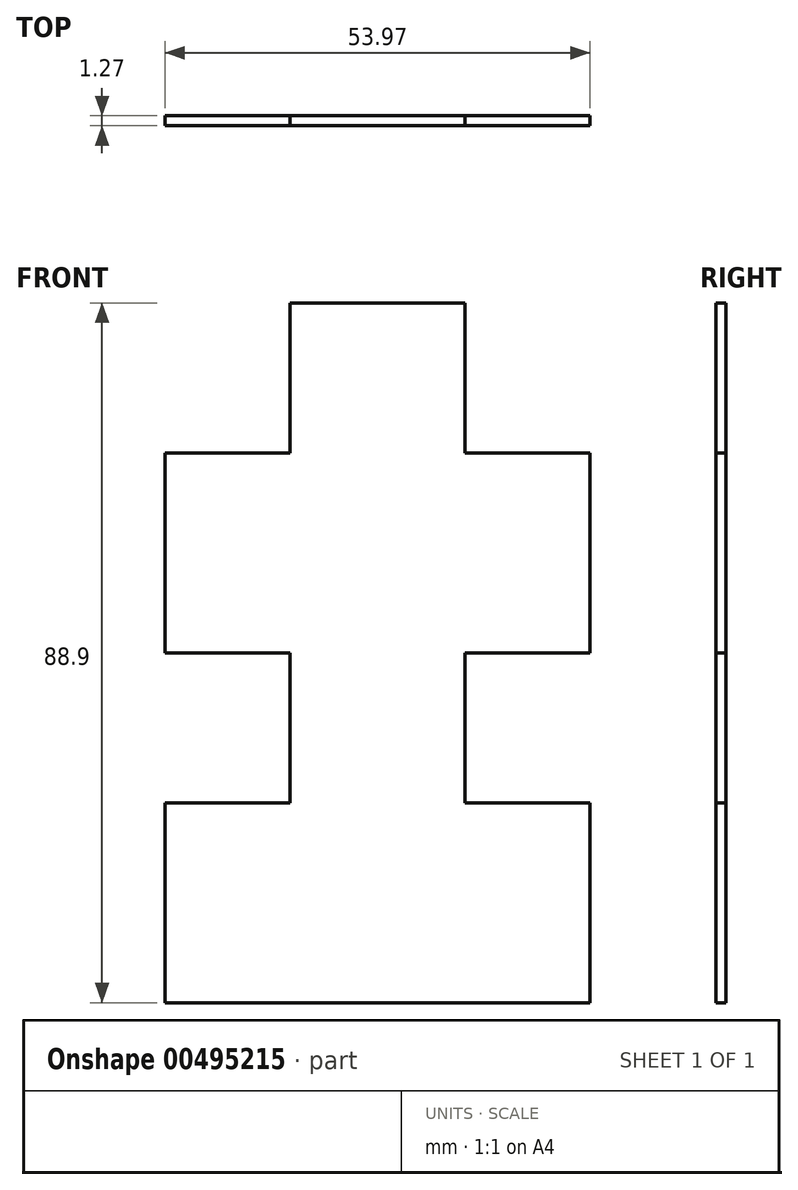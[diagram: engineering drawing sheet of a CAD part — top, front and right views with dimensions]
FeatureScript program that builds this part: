
annotation { "Feature Type Name" : "Feature", "Feature Type Description" : "" }
export const myFeature = defineFeature(function(context is Context, id is Id, definition is map)
    precondition{}
    {
        {
            var Q0;
            Q0=qCreatedBy(makeId("Front.planeOp"),FACE);
            var sketch = newSketch(context, id + "F0", { "sketchPlane" : qUnion([Q0])});
            skLineSegment(sketch, "E0", {"start": v(0.95, 45.3) * mm, "end": v(23.18, 45.3) * mm});
            skLineSegment(sketch, "E1", {"start": v(23.18, 45.3) * mm, "end": v(23.18, 26.25) * mm});
            skLineSegment(sketch, "E2", {"start": v(23.18, 26.25) * mm, "end": v(39.05, 26.25) * mm});
            skLineSegment(sketch, "E3", {"start": v(39.05, 26.25) * mm, "end": v(39.05, 0.85) * mm});
            skLineSegment(sketch, "E4", {"start": v(39.05, 0.85) * mm, "end": v(23.18, 0.85) * mm});
            skLineSegment(sketch, "E5", {"start": v(0.95, 45.3) * mm, "end": v(0.95, 26.25) * mm});
            skLineSegment(sketch, "E6", {"start": v(0.95, 26.25) * mm, "end": v(-14.92, 26.25) * mm});
            skLineSegment(sketch, "E7", {"start": v(-14.92, 26.25) * mm, "end": v(-14.92, 0.85) * mm});
            skLineSegment(sketch, "E8", {"start": v(-14.92, 0.85) * mm, "end": v(0.95, 0.85) * mm});
            skLineSegment(sketch, "E9", {"start": v(0.95, -43.6) * mm, "end": v(23.18, -43.6) * mm});
            skLineSegment(sketch, "E10", {"start": v(23.18, -18.2) * mm, "end": v(39.05, -18.2) * mm});
            skLineSegment(sketch, "E11", {"start": v(39.05, -18.2) * mm, "end": v(39.05, -43.6) * mm});
            skLineSegment(sketch, "E12", {"start": v(39.05, -43.6) * mm, "end": v(23.18, -43.6) * mm});
            skLineSegment(sketch, "E13", {"start": v(0.95, -18.2) * mm, "end": v(-14.92, -18.2) * mm});
            skLineSegment(sketch, "E14", {"start": v(-14.92, -18.2) * mm, "end": v(-14.92, -43.6) * mm});
            skLineSegment(sketch, "E15", {"start": v(-14.92, -43.6) * mm, "end": v(0.95, -43.6) * mm});
            skLineSegment(sketch, "E16", {"start": v(0.95, -18.2) * mm, "end": v(0.95, 0.85) * mm});
            skLineSegment(sketch, "E17", {"start": v(23.18, 0.85) * mm, "end": v(23.18, -18.2) * mm});
            skSolve(sketch);
        }
        {
            var Q0;
            Q0=makeQuery(id+"F0.imprint","IMPRINT",FACE,{"disambiguationData":[TD([[makeQuery(id+"F0.imprint","IMPRINT",EDGE,{"derivedFrom":sQuery(id+"F0.wireOp",EDGE,"E0")}),-1.0]])]});
            extrude(context, id + "F1", {"entities" : qUnion([Q0]), "depth" : 1.27 * mm});
        }
    });
